# Revit family: Legrand Flush-mounting cabinets RWN
name_source: partatom
category: Installations électriques
units: mm (PartAtom-declared; Revit-internal decimal feet)

## family parameters
Basée sur le plan de construction = Non
Conserver l'orientation des annotations = Non
Cote de connecteur circulaire = Utiliser le diamètre
Couper avec des vides une fois chargée = Non
Numéro OmniClass = 23.80.00.00
Partagée = Non
Point de calcul de pièce = Non
Titre OmniClass = Electric Power and Lighting
Toujours verticalement = Oui
Type d'élément = Normal

## types (12) — shared parameters
Fabricant = legrand
General Conditions of Use = https://export.legrand.com
Maximum permissible current = 63 A
Modèle = RWN
Number of modules per row = 12+2
Recessed depth = 90 mm  [stored 0.295276 ft]
Recessed width = 330 mm
URL = www.legrand.com
width = 350 mm  [stored 1.14829 ft]
zero-valued in all types: Elévation par défaut

## per-type parameters (varying)
- Flush-mounting cabinet RWN 12 modules Plastic door 602411: Assembly Plastic door 1R=Oui; Assembly Plastic door 2R=Non; Assembly Plastic door 3R=Non; Assembly Plastic door 4R=Non; Assembly glass metal door 1R=Non; Assembly glass metal door 2R=Non; Assembly glass metal door 3R=Non; Assembly glass metal door 4R=Non; Assembly metal door 1R=Non; Assembly metal door 2R=Non; Assembly metal door 3R=Non; Assembly metal door 4R=Non; Cabinet 602411=Oui; Cabinet 602412=Non; Cabinet 602413=Non; Cabinet 602414=Non; Cabinet 602421=Non; Cabinet 602422=Non; Cabinet 602423=Non; Cabinet 602424=Non; Cabinet 602431=Non; Cabinet 602432=Non; Cabinet 602433=Non; Cabinet 602434=Non; Number of rows=1; Plastic door=Oui; Recessed height=305 mm  [stored 1.00066 ft]; Terminal block E=12 connections Icc 6kA; Terminal block N=2X 6 connections Icc 6kA; glass metal door=Non; height=335 mm  [stored 1.09908 ft]; metal door=Non
- Flush-mounting cabinet RWN 24 modules Plastic door 602412: Assembly Plastic door 1R=Non; Assembly Plastic door 2R=Oui; Assembly Plastic door 3R=Non; Assembly Plastic door 4R=Non; Assembly glass metal door 1R=Non; Assembly glass metal door 2R=Non; Assembly glass metal door 3R=Non; Assembly glass metal door 4R=Non; Assembly metal door 1R=Non; Assembly metal door 2R=Non; Assembly metal door 3R=Non; Assembly metal door 4R=Non; Cabinet 602411=Non; Cabinet 602412=Oui; Cabinet 602413=Non; Cabinet 602414=Non; Cabinet 602421=Non; Cabinet 602422=Non; Cabinet 602423=Non; Cabinet 602424=Non; Cabinet 602431=Non; Cabinet 602432=Non; Cabinet 602433=Non; Cabinet 602434=Non; Number of rows=2; Plastic door=Oui; Recessed height=430 mm; Terminal block E=22 connections Icc 6kA; Terminal block N=3X 8 connections Icc 6kA; glass metal door=Non; height=460 mm  [stored 1.50919 ft]; metal door=Non
- Flush-mounting cabinet RWN 36 modules Plastic door 602413: Assembly Plastic door 1R=Non; Assembly Plastic door 2R=Non; Assembly Plastic door 3R=Oui; Assembly Plastic door 4R=Non; Assembly glass metal door 1R=Non; Assembly glass metal door 2R=Non; Assembly glass metal door 3R=Non; Assembly glass metal door 4R=Non; Assembly metal door 1R=Non; Assembly metal door 2R=Non; Assembly metal door 3R=Non; Assembly metal door 4R=Non; Cabinet 602411=Non; Cabinet 602412=Non; Cabinet 602413=Oui; Cabinet 602414=Non; Cabinet 602421=Non; Cabinet 602422=Non; Cabinet 602423=Non; Cabinet 602424=Non; Cabinet 602431=Non; Cabinet 602432=Non; Cabinet 602433=Non; Cabinet 602434=Non; Number of rows=3; Plastic door=Oui; Recessed height=555 mm  [stored 1.82087 ft]; Terminal block E=30 connections Icc 6kA; Terminal block N=4X 8 connections Icc 6kA; glass metal door=Non; height=585 mm  [stored 1.91929 ft]; metal door=Non
- Flush-mounting cabinet RWN 48 modules Plastic door 602414: Assembly Plastic door 1R=Non; Assembly Plastic door 2R=Non; Assembly Plastic door 3R=Non; Assembly Plastic door 4R=Oui; Assembly glass metal door 1R=Non; Assembly glass metal door 2R=Non; Assembly glass metal door 3R=Non; Assembly glass metal door 4R=Non; Assembly metal door 1R=Non; Assembly metal door 2R=Non; Assembly metal door 3R=Non; Assembly metal door 4R=Non; Cabinet 602411=Non; Cabinet 602412=Non; Cabinet 602413=Non; Cabinet 602414=Oui; Cabinet 602421=Non; Cabinet 602422=Non; Cabinet 602423=Non; Cabinet 602424=Non; Cabinet 602431=Non; Cabinet 602432=Non; Cabinet 602433=Non; Cabinet 602434=Non; Number of rows=4; Plastic door=Oui; Recessed height=680 mm  [stored 2.23097 ft]; Terminal block E=38 connections Icc 6kA; Terminal block N=5X 8 connections Icc 6kA; glass metal door=Non; height=710 mm  [stored 2.3294 ft]; metal door=Non
- Flush-mounting cabinet RWN 12 modules metal door  602431: Assembly Plastic door 1R=Non; Assembly Plastic door 2R=Non; Assembly Plastic door 3R=Non; Assembly Plastic door 4R=Non; Assembly glass metal door 1R=Non; Assembly glass metal door 2R=Non; Assembly glass metal door 3R=Non; Assembly glass metal door 4R=Non; Assembly metal door 1R=Oui; Assembly metal door 2R=Non; Assembly metal door 3R=Non; Assembly metal door 4R=Non; Cabinet 602411=Non; Cabinet 602412=Non; Cabinet 602413=Non; Cabinet 602414=Non; Cabinet 602421=Non; Cabinet 602422=Non; Cabinet 602423=Non; Cabinet 602424=Non; Cabinet 602431=Oui; Cabinet 602432=Non; Cabinet 602433=Non; Cabinet 602434=Non; Number of rows=1; Plastic door=Non; Recessed height=305 mm  [stored 1.00066 ft]; Terminal block E=12 connections Icc 6kA; Terminal block N=2X 6 connections Icc 6kA; glass metal door=Non; height=335 mm  [stored 1.09908 ft]; metal door=Oui
- Flush-mounting cabinet RWN 24 modules metal door  602432: Assembly Plastic door 1R=Non; Assembly Plastic door 2R=Non; Assembly Plastic door 3R=Non; Assembly Plastic door 4R=Non; Assembly glass metal door 1R=Non; Assembly glass metal door 2R=Non; Assembly glass metal door 3R=Non; Assembly glass metal door 4R=Non; Assembly metal door 1R=Non; Assembly metal door 2R=Oui; Assembly metal door 3R=Non; Assembly metal door 4R=Non; Cabinet 602411=Non; Cabinet 602412=Non; Cabinet 602413=Non; Cabinet 602414=Non; Cabinet 602421=Non; Cabinet 602422=Non; Cabinet 602423=Non; Cabinet 602424=Non; Cabinet 602431=Non; Cabinet 602432=Oui; Cabinet 602433=Non; Cabinet 602434=Non; Number of rows=2; Plastic door=Non; Recessed height=430 mm; Terminal block E=22 connections Icc 6kA; Terminal block N=3X 8 connections Icc 6kA; glass metal door=Non; height=460 mm  [stored 1.50919 ft]; metal door=Oui
- Flush-mounting cabinet RWN 36 modules metal door  602433: Assembly Plastic door 1R=Non; Assembly Plastic door 2R=Non; Assembly Plastic door 3R=Non; Assembly Plastic door 4R=Non; Assembly glass metal door 1R=Non; Assembly glass metal door 2R=Non; Assembly glass metal door 3R=Non; Assembly glass metal door 4R=Non; Assembly metal door 1R=Non; Assembly metal door 2R=Non; Assembly metal door 3R=Oui; Assembly metal door 4R=Non; Cabinet 602411=Non; Cabinet 602412=Non; Cabinet 602413=Non; Cabinet 602414=Non; Cabinet 602421=Non; Cabinet 602422=Non; Cabinet 602423=Non; Cabinet 602424=Non; Cabinet 602431=Non; Cabinet 602432=Non; Cabinet 602433=Oui; Cabinet 602434=Non; Number of rows=3; Plastic door=Non; Recessed height=555 mm  [stored 1.82087 ft]; Terminal block E=30 connections Icc 6kA; Terminal block N=4X 8 connections Icc 6kA; glass metal door=Non; height=585 mm  [stored 1.91929 ft]; metal door=Oui
- Flush-mounting cabinet RWN 48 modules metal door 602434: Assembly Plastic door 1R=Non; Assembly Plastic door 2R=Non; Assembly Plastic door 3R=Non; Assembly Plastic door 4R=Non; Assembly glass metal door 1R=Non; Assembly glass metal door 2R=Non; Assembly glass metal door 3R=Non; Assembly glass metal door 4R=Non; Assembly metal door 1R=Non; Assembly metal door 2R=Non; Assembly metal door 3R=Non; Assembly metal door 4R=Oui; Cabinet 602411=Non; Cabinet 602412=Non; Cabinet 602413=Non; Cabinet 602414=Non; Cabinet 602421=Non; Cabinet 602422=Non; Cabinet 602423=Non; Cabinet 602424=Non; Cabinet 602431=Non; Cabinet 602432=Non; Cabinet 602433=Non; Cabinet 602434=Oui; Number of rows=4; Plastic door=Non; Recessed height=680 mm  [stored 2.23097 ft]; Terminal block E=38 connections Icc 6kA; Terminal block N=5X 8 connections Icc 6kA; glass metal door=Non; height=710 mm  [stored 2.3294 ft]; metal door=Oui
- Flush-mounting cabinet RWN 12 modules transparent door 602421: Assembly Plastic door 1R=Non; Assembly Plastic door 2R=Non; Assembly Plastic door 3R=Non; Assembly Plastic door 4R=Non; Assembly glass metal door 1R=Oui; Assembly glass metal door 2R=Non; Assembly glass metal door 3R=Non; Assembly glass metal door 4R=Non; Assembly metal door 1R=Non; Assembly metal door 2R=Non; Assembly metal door 3R=Non; Assembly metal door 4R=Non; Cabinet 602411=Non; Cabinet 602412=Non; Cabinet 602413=Non; Cabinet 602414=Non; Cabinet 602421=Oui; Cabinet 602422=Non; Cabinet 602423=Non; Cabinet 602424=Non; Cabinet 602431=Non; Cabinet 602432=Non; Cabinet 602433=Non; Cabinet 602434=Non; Number of rows=1; Plastic door=Non; Recessed height=305 mm  [stored 1.00066 ft]; Terminal block E=12 connections Icc 6kA; Terminal block N=2X 6 connections Icc 6kA; glass metal door=Oui; height=335 mm  [stored 1.09908 ft]; metal door=Non
- Flush-mounting cabinet RWN 24 modules transparent door 602422: Assembly Plastic door 1R=Non; Assembly Plastic door 2R=Non; Assembly Plastic door 3R=Non; Assembly Plastic door 4R=Non; Assembly glass metal door 1R=Non; Assembly glass metal door 2R=Oui; Assembly glass metal door 3R=Non; Assembly glass metal door 4R=Non; Assembly metal door 1R=Non; Assembly metal door 2R=Non; Assembly metal door 3R=Non; Assembly metal door 4R=Non; Cabinet 602411=Non; Cabinet 602412=Non; Cabinet 602413=Non; Cabinet 602414=Non; Cabinet 602421=Non; Cabinet 602422=Oui; Cabinet 602423=Non; Cabinet 602424=Non; Cabinet 602431=Non; Cabinet 602432=Non; Cabinet 602433=Non; Cabinet 602434=Non; Number of rows=2; Plastic door=Non; Recessed height=430 mm; Terminal block E=22 connections Icc 6kA; Terminal block N=3X 8 connections Icc 6kA; glass metal door=Oui; height=460 mm  [stored 1.50919 ft]; metal door=Non
- Flush-mounting cabinet RWN 36 modules transparent door 602423: Assembly Plastic door 1R=Non; Assembly Plastic door 2R=Non; Assembly Plastic door 3R=Non; Assembly Plastic door 4R=Non; Assembly glass metal door 1R=Non; Assembly glass metal door 2R=Non; Assembly glass metal door 3R=Oui; Assembly glass metal door 4R=Non; Assembly metal door 1R=Non; Assembly metal door 2R=Non; Assembly metal door 3R=Non; Assembly metal door 4R=Non; Cabinet 602411=Non; Cabinet 602412=Non; Cabinet 602413=Non; Cabinet 602414=Non; Cabinet 602421=Non; Cabinet 602422=Non; Cabinet 602423=Oui; Cabinet 602424=Non; Cabinet 602431=Non; Cabinet 602432=Non; Cabinet 602433=Non; Cabinet 602434=Non; Number of rows=3; Plastic door=Non; Recessed height=555 mm  [stored 1.82087 ft]; Terminal block E=30 connections Icc 6kA; Terminal block N=4X 8 connections Icc 6kA; glass metal door=Oui; height=585 mm  [stored 1.91929 ft]; metal door=Non
- Flush-mounting cabinet RWN 48 modules transparent door 602424: Assembly Plastic door 1R=Non; Assembly Plastic door 2R=Non; Assembly Plastic door 3R=Non; Assembly Plastic door 4R=Non; Assembly glass metal door 1R=Non; Assembly glass metal door 2R=Non; Assembly glass metal door 3R=Non; Assembly glass metal door 4R=Oui; Assembly metal door 1R=Non; Assembly metal door 2R=Non; Assembly metal door 3R=Non; Assembly metal door 4R=Non; Cabinet 602411=Non; Cabinet 602412=Non; Cabinet 602413=Non; Cabinet 602414=Non; Cabinet 602421=Non; Cabinet 602422=Non; Cabinet 602423=Non; Cabinet 602424=Oui; Cabinet 602431=Non; Cabinet 602432=Non; Cabinet 602433=Non; Cabinet 602434=Non; Number of rows=4; Plastic door=Non; Recessed height=680 mm  [stored 2.23097 ft]; Terminal block E=38 connections Icc 6kA; Terminal block N=5X 8 connections Icc 6kA; glass metal door=Oui; height=710 mm  [stored 2.3294 ft]; metal door=Non

note: [stored X ft] marks values corroborated as IEEE doubles in the binary element streams (Revit-internal decimal feet)
